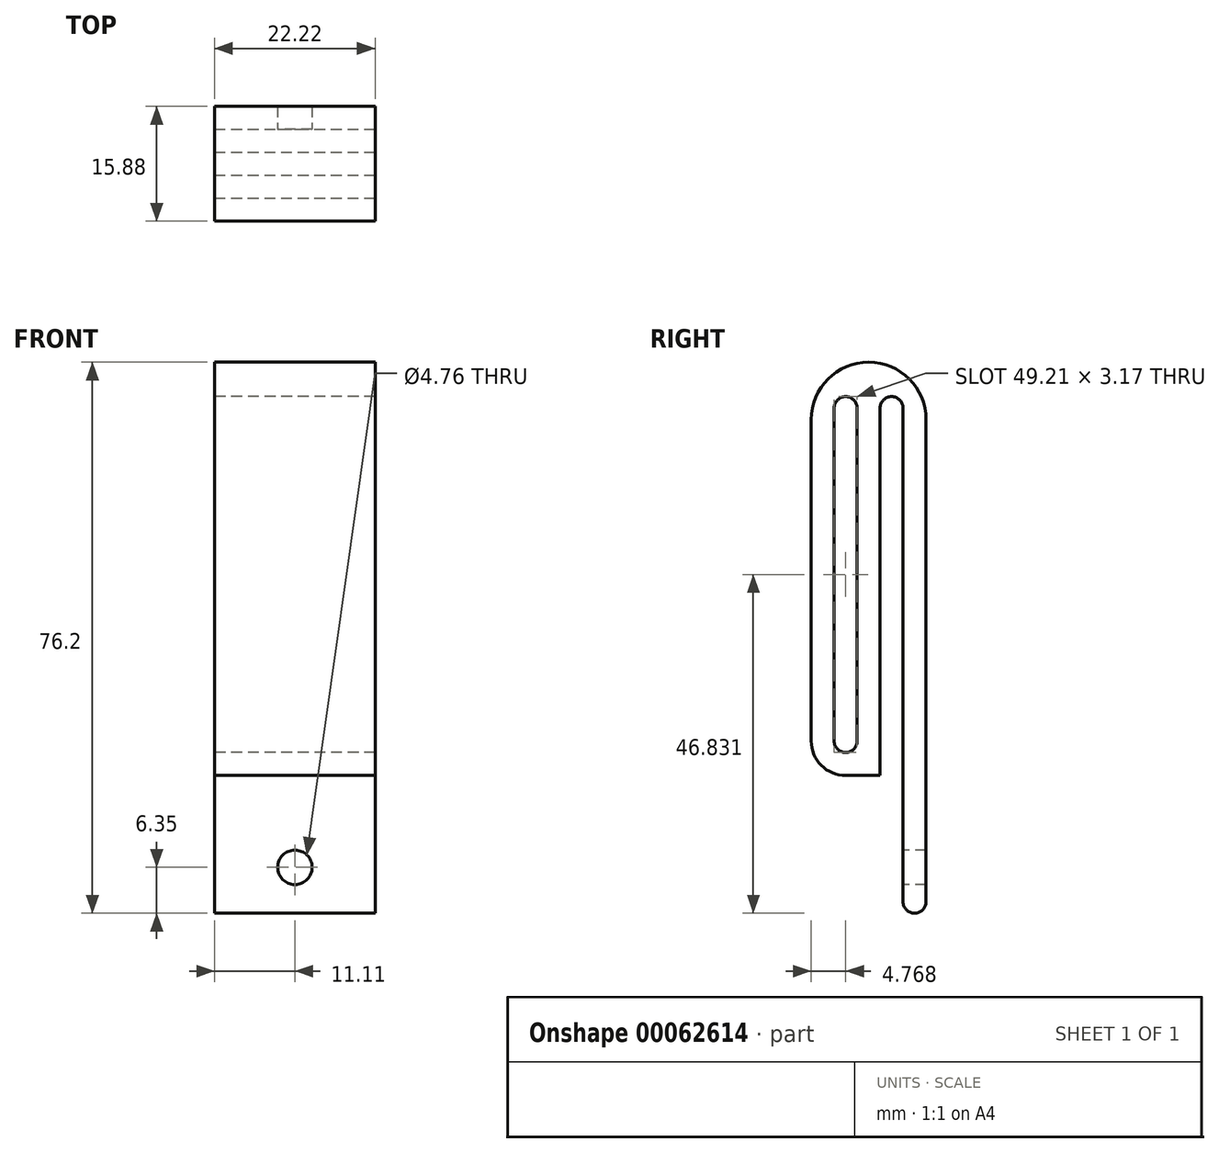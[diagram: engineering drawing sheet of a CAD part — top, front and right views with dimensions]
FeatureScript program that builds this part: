
annotation { "Feature Type Name" : "Feature", "Feature Type Description" : "" }
export const myFeature = defineFeature(function(context is Context, id is Id, definition is map)
    precondition{}
    {
        {
            var Q0;
            Q0=qCreatedBy(makeId("Front.planeOp"),FACE);
            var sketch = newSketch(context, id + "F8", { "sketchPlane" : qUnion([Q0])});
            skLineSegment(sketch, "E0.rect.bottom", {"start": v(-11.11, -38.1) * mm, "end": v(11.11, -38.1) * mm});
            skLineSegment(sketch, "E0.rect.top", {"start": v(-11.11, 38.1) * mm, "end": v(11.11, 38.1) * mm});
            skLineSegment(sketch, "E0.rect.left", {"start": v(-11.11, -38.1) * mm, "end": v(-11.11, 38.1) * mm});
            skLineSegment(sketch, "E0.rect.right", {"start": v(11.11, -38.1) * mm, "end": v(11.11, 38.1) * mm});
            skPoint(sketch, "E0.rect.middle", {"position": v(0, 0) * mm});
            skSolve(sketch);
        }
        {
            var Q0;
            Q0=makeQuery(id+"F8.imprint","IMPRINT",FACE,{"disambiguationData":[TD([[makeQuery(id+"F8.imprint","IMPRINT",EDGE,{"derivedFrom":sQuery(id+"F8.wireOp",EDGE,"E0.rect.bottom")}),1.0]])]});
            extrude(context, id + "F9", {"entities" : qUnion([Q0]), "depth" : 3.17 * mm});
        }
        {
            var Q0;
            Q0=makeQuery(id+"F9.opExtrude","CAP_FACE",FACE,{"disambiguationData":[OSD([sQuery(id+"F8.wireOp",EDGE,"E0.rect.bottom"),sQuery(id+"F8.wireOp",EDGE,"E0.rect.top"),sQuery(id+"F8.wireOp",EDGE,"E0.rect.left"),sQuery(id+"F8.wireOp",EDGE,"E0.rect.right")])],"isStart":false});
            var sketch = newSketch(context, id + "F0", { "sketchPlane" : qUnion([Q0])});
            skLineSegment(sketch, "E1.bottom", {"start": v(-11.11, 38.1) * mm, "end": v(11.11, 38.1) * mm});
            skLineSegment(sketch, "E1.top", {"start": v(-11.11, -19.05) * mm, "end": v(11.11, -19.05) * mm});
            skLineSegment(sketch, "E1.left", {"start": v(-11.11, 38.1) * mm, "end": v(-11.11, -19.05) * mm});
            skLineSegment(sketch, "E1.right", {"start": v(11.11, 38.1) * mm, "end": v(11.11, -19.05) * mm});
            skSolve(sketch);
        }
        {
            var Q0;
            Q0=makeQuery(id+"F0.imprint","IMPRINT",FACE,{"disambiguationData":[TD([[makeQuery(id+"F0.imprint","IMPRINT",EDGE,{"derivedFrom":sQuery(id+"F0.wireOp",EDGE,"E1.bottom")}),-1.0]])]});
            extrude(context, id + "F10", {"entities" : qUnion([Q0]), "operationType" : NewBodyOperationType.ADD, "depth" : 12.7 * mm});
        }
        {
            var Q0;
            Q0=makeQuery(id+"F9.opExtrude","CAP_FACE",FACE,{"disambiguationData":[OSD([sQuery(id+"F8.wireOp",EDGE,"E0.rect.bottom"),sQuery(id+"F8.wireOp",EDGE,"E0.rect.top"),sQuery(id+"F8.wireOp",EDGE,"E0.rect.left"),sQuery(id+"F8.wireOp",EDGE,"E0.rect.right")])],"isStart":false});
            var sketch = newSketch(context, id + "F1", { "sketchPlane" : qUnion([Q0])});
            skCircle(sketch, "E2", {"center": v(0, -31.75) * mm, "radius": 2.38 * mm});
            skSolve(sketch);
        }
        {
            var Q0;
            Q0=makeQuery(id+"F1.imprint","IMPRINT",FACE,{"disambiguationData":[TD([[makeQuery(id+"F1.imprint","IMPRINT",EDGE,{"derivedFrom":sQuery(id+"F1.wireOp",EDGE,"E2")}),1.0]])]});
            extrude(context, id + "F2", {"entities" : qUnion([Q0]), "operationType" : NewBodyOperationType.REMOVE, "endBound" : BoundingType.UP_TO_NEXT, "oppositeDirection" : true, "depth" : 25.4 * mm});
        }
        {
            var Q0;
            Q0=makeQuery(id+"F10.boolean.opBoolean","MERGE",FACE,{"derivedFrom":[makeQuery(id+"F9.opExtrude","SWEPT_FACE",FACE,{"disambiguationData":[OSD([sQuery(id+"F8.wireOp",EDGE,"E0.rect.right")])]}),makeQuery(id+"F10.opExtrude","SWEPT_FACE",FACE,{"disambiguationData":[OSD([sQuery(id+"F0.wireOp",EDGE,"E1.right")])]})]});
            var sketch = newSketch(context, id + "F3", { "sketchPlane" : qUnion([Q0])});
            skLineSegment(sketch, "E3", {"start": v(-3.18, -19.05) * mm, "end": v(-3.18, 38.1) * mm, "construction": true});
            skLineSegment(sketch, "E4", {"start": v(-15.88, 33.34) * mm, "end": v(0, 33.34) * mm, "construction": true});
            skLineSegment(sketch, "E5", {"start": v(-15.88, -15.88) * mm, "end": v(0, -15.88) * mm, "construction": true});
            skLineSegment(sketch, "E6", {"start": v(-12.7, 38.1) * mm, "end": v(-12.7, -19.05) * mm, "construction": true});
            skLineSegment(sketch, "E7.bottom", {"start": v(-12.7, 33.34) * mm, "end": v(-9.53, 33.34) * mm});
            skLineSegment(sketch, "E7.top", {"start": v(-12.7, -15.88) * mm, "end": v(-9.52, -15.88) * mm});
            skLineSegment(sketch, "E7.left", {"start": v(-12.7, 33.34) * mm, "end": v(-12.7, -15.88) * mm});
            skLineSegment(sketch, "E7.right", {"start": v(-9.53, 33.34) * mm, "end": v(-9.52, -15.88) * mm});
            skLineSegment(sketch, "E8.bottom", {"start": v(-3.18, 33.34) * mm, "end": v(-6.35, 33.34) * mm});
            skLineSegment(sketch, "E8.top", {"start": v(-3.18, -19.05) * mm, "end": v(-6.35, -19.05) * mm});
            skLineSegment(sketch, "E8.left", {"start": v(-3.18, 33.34) * mm, "end": v(-3.18, -19.05) * mm});
            skLineSegment(sketch, "E8.right", {"start": v(-6.35, 33.34) * mm, "end": v(-6.35, -19.05) * mm});
            skSolve(sketch);
        }
        {
            var Q0;
            Q0=makeQuery(id+"F3.imprint","IMPRINT",FACE,{"disambiguationData":[TD([[makeQuery(id+"F3.imprint","IMPRINT",EDGE,{"derivedFrom":sQuery(id+"F3.wireOp",EDGE,"E7.bottom")}),-1.0]])]});
            var Q1;
            Q1=makeQuery(id+"F3.imprint","IMPRINT",FACE,{"disambiguationData":[TD([[makeQuery(id+"F3.imprint","IMPRINT",EDGE,{"derivedFrom":sQuery(id+"F3.wireOp",EDGE,"E8.bottom")}),1.0]])]});
            extrude(context, id + "F4", {"entities" : qUnion([Q0, Q1]), "operationType" : NewBodyOperationType.REMOVE, "endBound" : BoundingType.UP_TO_NEXT, "oppositeDirection" : true, "depth" : 25.4 * mm});
        }
        {
            var Q0;
            Q0=makeQuery(id+"F4.boolean.opBoolean","COPY",EDGE,{"derivedFrom":makeQuery(id+"F4.opExtrude","SWEPT_EDGE",EDGE,{"disambiguationData":[OSD([sQuery(id+"F3.wireOp",EDGE,"E7.bottom"),sQuery(id+"F3.wireOp",EDGE,"E7.left")])]})});
            var Q1;
            Q1=makeQuery(id+"F4.boolean.opBoolean","COPY",EDGE,{"derivedFrom":makeQuery(id+"F4.opExtrude","SWEPT_EDGE",EDGE,{"disambiguationData":[OSD([sQuery(id+"F3.wireOp",EDGE,"E8.bottom"),sQuery(id+"F3.wireOp",EDGE,"E8.right")])]})});
            var Q2;
            Q2=makeQuery(id+"F4.boolean.opBoolean","COPY",EDGE,{"derivedFrom":makeQuery(id+"F4.opExtrude","SWEPT_EDGE",EDGE,{"disambiguationData":[OSD([sQuery(id+"F3.wireOp",EDGE,"E7.bottom"),sQuery(id+"F3.wireOp",EDGE,"E7.right")])]})});
            var Q3;
            Q3=makeQuery(id+"F4.boolean.opBoolean","COPY",EDGE,{"derivedFrom":makeQuery(id+"F4.opExtrude","SWEPT_EDGE",EDGE,{"disambiguationData":[OSD([sQuery(id+"F3.wireOp",EDGE,"E8.bottom"),sQuery(id+"F3.wireOp",EDGE,"E8.left")])]})});
            var Q4;
            Q4=makeQuery(id+"F4.boolean.opBoolean","COPY",EDGE,{"derivedFrom":makeQuery(id+"F4.opExtrude","SWEPT_EDGE",EDGE,{"disambiguationData":[OSD([sQuery(id+"F3.wireOp",EDGE,"E7.top"),sQuery(id+"F3.wireOp",EDGE,"E7.left")])]})});
            var Q5;
            Q5=makeQuery(id+"F4.boolean.opBoolean","COPY",EDGE,{"derivedFrom":makeQuery(id+"F4.opExtrude","SWEPT_EDGE",EDGE,{"disambiguationData":[OSD([sQuery(id+"F3.wireOp",EDGE,"E7.top"),sQuery(id+"F3.wireOp",EDGE,"E7.right")])]})});
            var Q6;
            Q6=makeQuery(id+"F9.opExtrude","CAP_EDGE",EDGE,{"disambiguationData":[OSD([sQuery(id+"F8.wireOp",EDGE,"E0.rect.bottom")])],"isStart":true});
            var Q7;
            Q7=makeQuery(id+"F9.opExtrude","CAP_EDGE",EDGE,{"disambiguationData":[OSD([sQuery(id+"F8.wireOp",EDGE,"E0.rect.bottom")])],"isStart":false});
            fillet(context, id + "F5", {"entities" : qUnion([Q0, Q1, Q2, Q3, Q4, Q5, Q6, Q7]), "radius" : 1.59 * mm, "tangentPropagation" : true, "allowEdgeOverflow" : false});
        }
        {
            var Q0;
            Q0=makeQuery(id+"F10.opExtrude","CAP_EDGE",EDGE,{"disambiguationData":[OSD([sQuery(id+"F0.wireOp",EDGE,"E1.bottom")])],"isStart":false});
            var Q1;
            Q1=makeQuery(id+"F9.opExtrude","CAP_EDGE",EDGE,{"disambiguationData":[OSD([sQuery(id+"F8.wireOp",EDGE,"E0.rect.top")])],"isStart":true});
            fillet(context, id + "F6", {"entities" : qUnion([Q0, Q1]), "radius" : 7.94 * mm, "tangentPropagation" : true, "allowEdgeOverflow" : false});
        }
        {
            var Q0;
            Q0=makeQuery(id+"F10.opExtrude","CAP_EDGE",EDGE,{"disambiguationData":[OSD([sQuery(id+"F0.wireOp",EDGE,"E1.top")])],"isStart":false});
            var Q1;
            Q1=makeQuery(id+"F4.boolean.opBoolean","COPY",EDGE,{"derivedFrom":makeQuery(id+"F4.opExtrude","SWEPT_EDGE",EDGE,{"disambiguationData":[OSD([sQuery(id+"F8.wireOp",EDGE,"E0.rect.right"),sQuery(id+"F0.wireOp",EDGE,"E1.top"),sQuery(id+"F0.wireOp",EDGE,"E1.right"),sQuery(id+"F3.wireOp",EDGE,"E8.top"),sQuery(id+"F3.wireOp",EDGE,"E8.right")])]})});
            fillet(context, id + "F7", {"entities" : qUnion([Q0, Q1]), "radius" : 4.76 * mm, "tangentPropagation" : true, "allowEdgeOverflow" : false});
        }
    });
